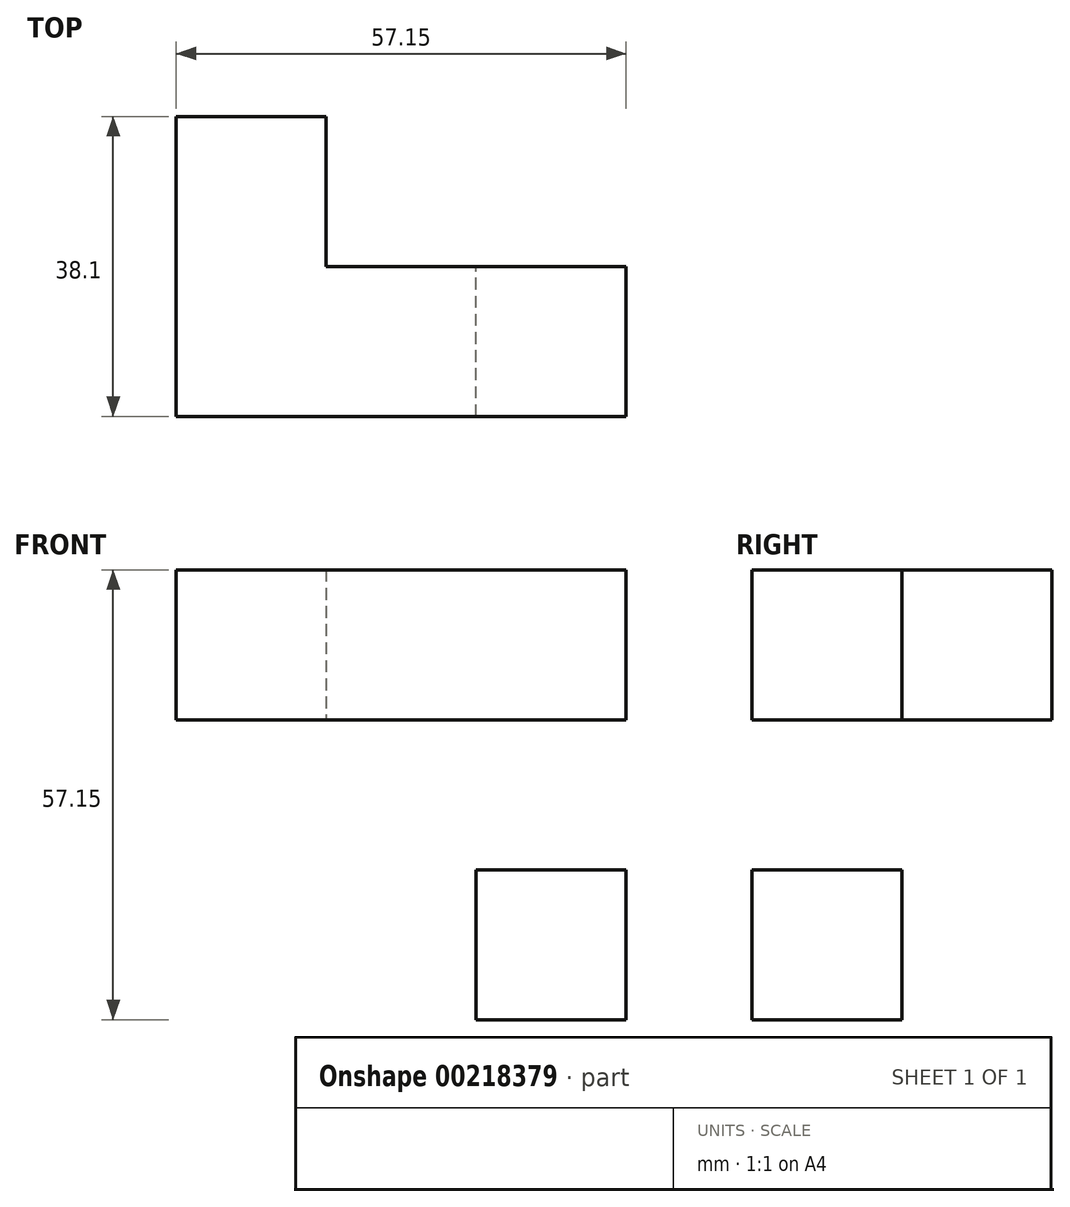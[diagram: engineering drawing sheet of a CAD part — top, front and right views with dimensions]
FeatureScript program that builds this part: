
annotation { "Feature Type Name" : "Feature", "Feature Type Description" : "" }
export const myFeature = defineFeature(function(context is Context, id is Id, definition is map)
    precondition{}
    {
        {
            var Q0;
            Q0=qCreatedBy(makeId("Front.planeOp"),FACE);
            var sketch = newSketch(context, id + "F0", { "sketchPlane" : qUnion([Q0])});
            skLineSegment(sketch, "E0.bottom", {"start": v(-58.6, 45.18) * mm, "end": v(-39.55, 45.18) * mm});
            skLineSegment(sketch, "E0.top", {"start": v(-58.6, 26.13) * mm, "end": v(-39.55, 26.13) * mm});
            skLineSegment(sketch, "E0.left", {"start": v(-58.6, 45.18) * mm, "end": v(-58.6, 26.13) * mm});
            skLineSegment(sketch, "E0.right", {"start": v(-39.55, 45.18) * mm, "end": v(-39.55, 26.13) * mm});
            skLineSegment(sketch, "E1.bottom", {"start": v(-39.55, 45.18) * mm, "end": v(-20.5, 45.18) * mm});
            skLineSegment(sketch, "E1.top", {"start": v(-39.55, 26.13) * mm, "end": v(-20.5, 26.13) * mm});
            skLineSegment(sketch, "E1.right", {"start": v(-20.5, 45.18) * mm, "end": v(-20.5, 26.13) * mm});
            skLineSegment(sketch, "E2.bottom", {"start": v(-20.5, 45.18) * mm, "end": v(-1.45, 45.18) * mm});
            skLineSegment(sketch, "E2.top", {"start": v(-20.5, 26.13) * mm, "end": v(-1.45, 26.13) * mm});
            skLineSegment(sketch, "E2.right", {"start": v(-1.45, 45.18) * mm, "end": v(-1.45, 26.13) * mm});
            skLineSegment(sketch, "E3.bottom", {"start": v(-20.5, 7.08) * mm, "end": v(-1.45, 7.08) * mm});
            skLineSegment(sketch, "E3.left", {"start": v(-20.5, 7.08) * mm, "end": v(-20.5, 26.13) * mm});
            skLineSegment(sketch, "E3.right", {"start": v(-1.45, 7.08) * mm, "end": v(-1.45, 26.13) * mm});
            skLineSegment(sketch, "E4.bottom", {"start": v(-20.5, -11.97) * mm, "end": v(-1.45, -11.97) * mm});
            skLineSegment(sketch, "E4.left", {"start": v(-20.5, -11.97) * mm, "end": v(-20.5, 7.08) * mm});
            skLineSegment(sketch, "E4.right", {"start": v(-1.45, -11.97) * mm, "end": v(-1.45, 7.08) * mm});
            skSolve(sketch);
        }
        {
            var Q0;
            Q0=makeQuery(id+"F0.imprint","IMPRINT",FACE,{"disambiguationData":[TD([[makeQuery(id+"F0.imprint","IMPRINT",EDGE,{"derivedFrom":sQuery(id+"F0.wireOp",EDGE,"E0.bottom")}),-1.0]])]});
            var Q1;
            Q1=makeQuery(id+"F0.imprint","IMPRINT",FACE,{"disambiguationData":[TD([[makeQuery(id+"F0.imprint","IMPRINT",EDGE,{"derivedFrom":sQuery(id+"F0.wireOp",EDGE,"E1.bottom")}),-1.0]])]});
            var Q2;
            Q2=makeQuery(id+"F0.imprint","IMPRINT",FACE,{"disambiguationData":[TD([[makeQuery(id+"F0.imprint","IMPRINT",EDGE,{"derivedFrom":sQuery(id+"F0.wireOp",EDGE,"E2.bottom")}),-1.0]])]});
            var Q3;
            Q3=makeQuery(id+"F0.imprint","IMPRINT",FACE,{"disambiguationData":[TD([[makeQuery(id+"F0.imprint","IMPRINT",EDGE,{"derivedFrom":sQuery(id+"F0.wireOp",EDGE,"E2.top")}),-1.0]])]});
            var Q4;
            Q4=makeQuery(id+"F0.imprint","IMPRINT",FACE,{"disambiguationData":[TD([[makeQuery(id+"F0.imprint","IMPRINT",EDGE,{"derivedFrom":sQuery(id+"F0.wireOp",EDGE,"E4.bottom")}),1.0]])]});
            extrude(context, id + "F1", {"entities" : qUnion([Q0, Q1, Q2, Q3, Q4]), "depth" : 19.05 * mm});
        }
        {
            var Q0;
            Q0=makeQuery(id+"F1.opExtrude","CAP_FACE",FACE,{"disambiguationData":[OSD([sQuery(id+"F0.wireOp",EDGE,"E0.bottom"),sQuery(id+"F0.wireOp",EDGE,"E0.top"),sQuery(id+"F0.wireOp",EDGE,"E0.left"),sQuery(id+"F0.wireOp",EDGE,"E1.bottom"),sQuery(id+"F0.wireOp",EDGE,"E1.top"),sQuery(id+"F0.wireOp",EDGE,"E2.bottom"),sQuery(id+"F0.wireOp",EDGE,"E2.right"),sQuery(id+"F0.wireOp",EDGE,"E3.left"),sQuery(id+"F0.wireOp",EDGE,"E3.right"),sQuery(id+"F0.wireOp",EDGE,"E4.bottom"),sQuery(id+"F0.wireOp",EDGE,"E4.left"),sQuery(id+"F0.wireOp",EDGE,"E4.right")])],"isStart":true});
            var sketch = newSketch(context, id + "F2", { "sketchPlane" : qUnion([Q0])});
            skLineSegment(sketch, "E5.bottom", {"start": v(58.6, 45.18) * mm, "end": v(39.55, 45.18) * mm});
            skLineSegment(sketch, "E5.top", {"start": v(58.6, 26.13) * mm, "end": v(39.55, 26.13) * mm});
            skLineSegment(sketch, "E5.left", {"start": v(58.6, 45.18) * mm, "end": v(58.6, 26.13) * mm});
            skLineSegment(sketch, "E5.right", {"start": v(39.55, 45.18) * mm, "end": v(39.55, 26.13) * mm});
            skSolve(sketch);
        }
        {
            var Q0;
            Q0=makeQuery(id+"F2.imprint","IMPRINT",FACE,{"disambiguationData":[TD([[makeQuery(id+"F2.imprint","IMPRINT",EDGE,{"derivedFrom":sQuery(id+"F2.wireOp",EDGE,"E5.bottom")}),1.0]])]});
            extrude(context, id + "F3", {"entities" : qUnion([Q0]), "operationType" : NewBodyOperationType.ADD, "depth" : 19.05 * mm});
        }
    });
